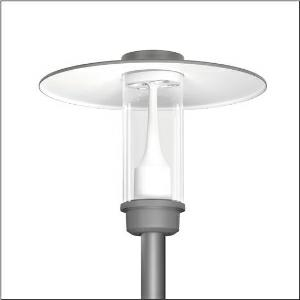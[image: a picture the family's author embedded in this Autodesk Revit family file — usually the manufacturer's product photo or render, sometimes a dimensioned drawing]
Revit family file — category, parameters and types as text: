
# Revit family: litepole_2_iq___st1_2a_5xa5425ef14h000022_7f5b
name_source: partatom
category: Lighting Fixtures
units: mm (PartAtom-declared; Revit-internal decimal feet)

## family parameters
Cut with Voids When Loaded = No
Host = Face
Light Source = No
Part Type = Normal
Room Calculation Point = No
Round Connector Dimension = Use Diameter
Shared = No

## types (1)
- --- (1 x LED, 1550 lm, 10.5 W, 3000K)
    Apparent Load = 11 VA
    CIE Flux Codes = 22 60 92 98 100
    Color Rendering = 70
    Color Temperature = 3000K
    Default Elevation = 1800 mm
    Description = Litepole 2 iQ, mast luminaire, Module 540 iQ-SR, primary light control with 3 zone facetted reflector, of plastic, silver coated, highly specular, structured, primary optical cover: cover, of PMMA, transparent, light distribution: ST1.2a, light emission: direct distribution, primary light characteristic: asymmetric, installation type: post-top, LED, High Power LED, rated luminous flux: 1.550lm, luminous efficacy: 148lm/W, light colour: 730, colour temperature: 3000K, control gear: iQ Street-Remote, control: Street-Remote, Auto-Match, Temp-Guard, Lumen-Switch, Night-Set, Smart-Wire, Light-Fading, Desk-Remote (wireless, voltage-free reading and setting of iQ features in the workshop via application-optimized NFC function/RFID function), optimised constant luminous flux control (CLO 2.0), pre-setting: logarithmic dimming characteristic, mains connection: 230..240V, AC, 50/60Hz, connection cable pre-assembled, cable length: 5,5m, wiring characteristics: H07RN-F, start of lifetime: 11W, end of service life: 11W, reduction: 5W, luminaire housing, upper part, of aluminium, coated, Siteco® metallic grey (DB 702S), diameter: 750mm, height: 590mm, spigot size: d x l = 76 x 70mm (post-top) | with reducer (optional accessory) 60 x 70mm, mounting height: 3..5m, post-top mast mounting element, of diecast aluminium, coated, Siteco® metallic grey (DB 702S), Module 540 iQ-SR, traffic white (RAL 9016), equipment: standard, protection rating (complete): IP65, insulation class (complete): insulation class II (safety insulation), certification: CE, ENEC, VDE, packaging unit: 1 piece

Light Distribution: ST1.2a
    Height = 590 mm
    Lamp = 1 x LED
    Lamp Light Flux = 1550 lm
    Lamp Power = 10.5 W
    Lamp count = 1
    Length = 750 mm
    Luminous efficacy = 148 lm/W
    Manufacturer = Siteco
    ModVariant = No
    Model = 5XA5425EF14H000022
    Number of Poles = 1
    OnlyDefault = Yes
    Power Factor = 1
    Product Name = Litepole 2 iQ | ST1.2a
    Product group = mast luminaire | pylon top
    ProductGroupID = 6100
    Protection Class = Protection class II
    Protection Degree = IP 65
    RLX_Detail_Level = 1
    RLX_Emergency_Light_Flux = 0 lm
    RLX_Emergency_Type = 0
    RLX_Emergency_Type_DB = No
    RlxData = <blob elided: 30965 chars, md5=a2f2aac9>
    Socket = socket
    Standby Power = 0 W
    System Light Flux = 1550 lm
    System Power = 11 W
    Type Comments = factory setting: luminous flux: 100 % | dim-lin: 254 | 419 mA
    Type Image = l_1006518.jpg
    URL = http://relux.com
    VarID = @adj_192578
    Voltage = 0 V
    Weight = 0.00 kg
    Width = 0 mm  [stored 0 ft]

note: [stored X ft] marks values corroborated as IEEE doubles in the binary element streams (Revit-internal decimal feet)

## geometry (parser evidence)
native form markers: Blend x4, Sweep x10
no freeform markers — native parametric forms only
